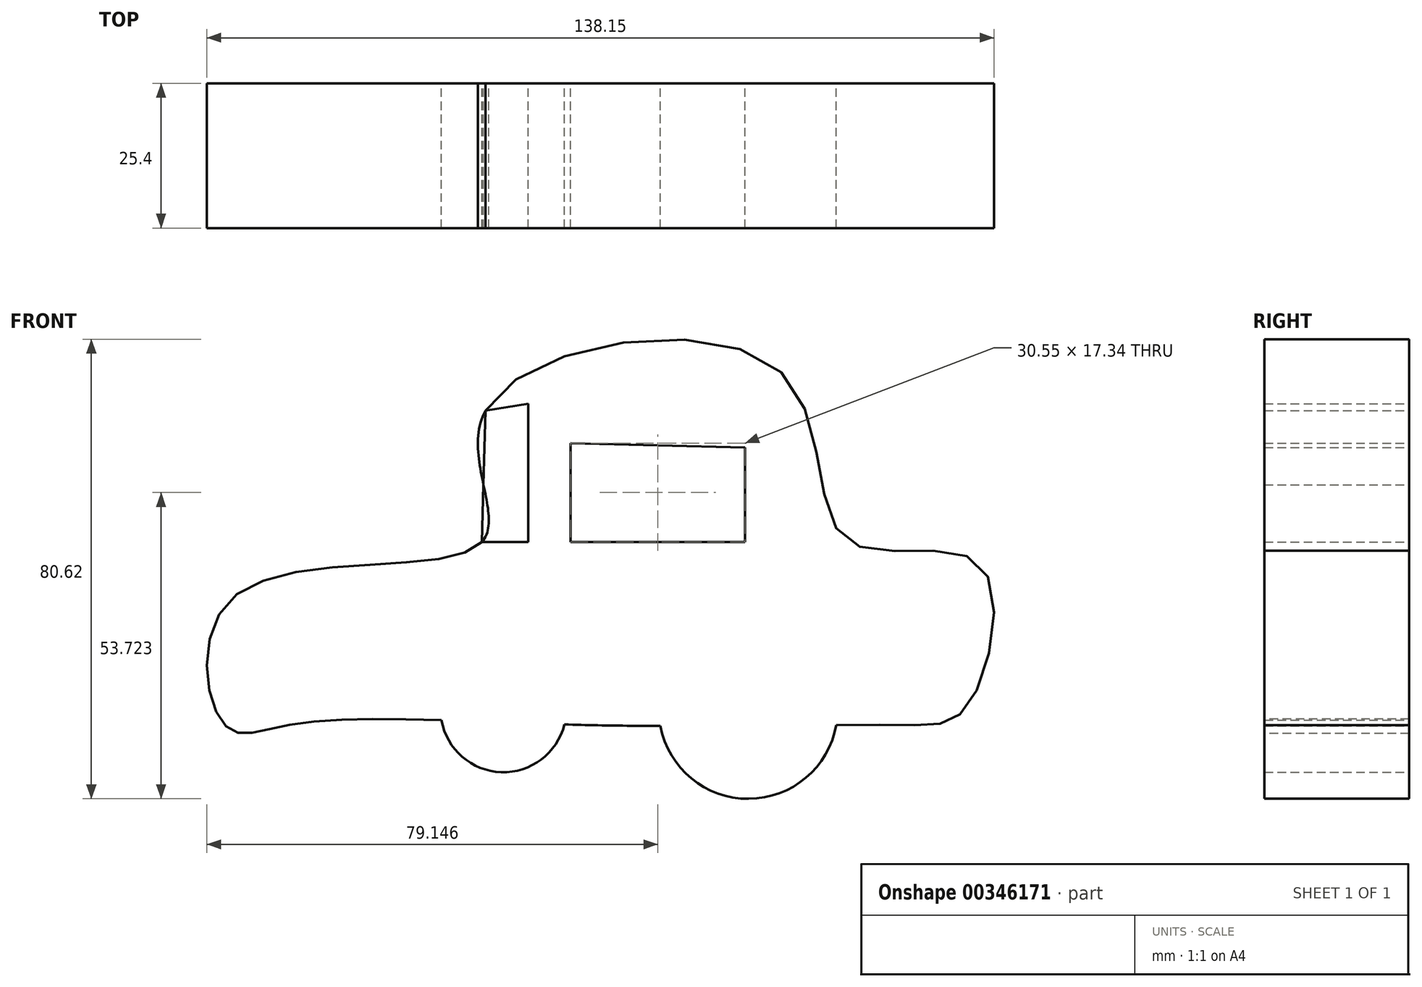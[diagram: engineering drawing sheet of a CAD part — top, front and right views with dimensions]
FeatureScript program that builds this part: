
annotation { "Feature Type Name" : "Feature", "Feature Type Description" : "" }
export const myFeature = defineFeature(function(context is Context, id is Id, definition is map)
    precondition{}
    {
        {
            var Q0;
            Q0=qCreatedBy(makeId("Front.planeOp"),FACE);
            var sketch = newSketch(context, id + "F0", { "sketchPlane" : qUnion([Q0])});
            skFitSpline(sketch, "E0", {"points": [v(-75.67, 0) * mm, v(-73.9, 22.66) * mm, v(-30.55, 32.12) * mm, v(-29.95, 55.18) * mm, v(21.09, 62.67) * mm, v(33.3, 32.52) * mm, v(56.56, 28.38) * mm, v(54.79, 3.55) * mm, v(43.55, 0) * mm, v(-11.82, 0) * mm, v(-64.44, 0) * mm, v(-75.67, 0) * mm]});
            skCircle(sketch, "E1", {"center": v(-26.8, 2.76) * mm, "radius": 11.03 * mm});
            skCircle(sketch, "E2", {"center": v(16.16, 2.76) * mm, "radius": 15.7 * mm});
            skLineSegment(sketch, "E3", {"start": v(-30.55, 32.12) * mm, "end": v(-22.47, 32.12) * mm});
            skLineSegment(sketch, "E4", {"start": v(-22.47, 32.12) * mm, "end": v(-22.47, 56.36) * mm});
            skLineSegment(sketch, "E5", {"start": v(-22.47, 56.36) * mm, "end": v(-29.95, 55.18) * mm});
            skLineSegment(sketch, "E6", {"start": v(-29.95, 55.18) * mm, "end": v(-30.55, 32.12) * mm});
            skLineSegment(sketch, "E7", {"start": v(-14.98, 49.46) * mm, "end": v(-14.98, 32.12) * mm});
            skLineSegment(sketch, "E8", {"start": v(-14.98, 32.12) * mm, "end": v(15.57, 32.12) * mm});
            skLineSegment(sketch, "E9", {"start": v(15.57, 32.12) * mm, "end": v(15.57, 48.68) * mm});
            skLineSegment(sketch, "E10", {"start": v(15.57, 48.68) * mm, "end": v(-14.98, 49.46) * mm});
            skSolve(sketch);
        }
        {
            var Q0;
            {var subQ0=sQuery(id+"F0.wireOp",EDGE,"E6");var subQ1=sQuery(id+"F0.wireOp",EDGE,"E0");var subQ3=makeQuery(id+"F0.imprint","INTERSECT",VERTEX,{"derivedFrom":[subQ1,subQ0]});Q0=makeQuery(id+"F0.imprint","IMPRINT",FACE,{"disambiguationData":[TD([[makeQuery(id+"F0.imprint","IMPRINT",EDGE,{"disambiguationData":[TD([[subQ3,1.0]])],"derivedFrom":subQ1}),1.0]])]});}
            var Q1;
            {var subQ0=sQuery(id+"F0.wireOp",EDGE,"E6");var subQ1=sQuery(id+"F0.wireOp",EDGE,"E0");var subQ3=makeQuery(id+"F0.imprint","INTERSECT",VERTEX,{"derivedFrom":[subQ1,subQ0]});Q1=makeQuery(id+"F0.imprint","IMPRINT",FACE,{"disambiguationData":[TD([[makeQuery(id+"F0.imprint","IMPRINT",EDGE,{"disambiguationData":[TD([[subQ3,-1.0]])],"derivedFrom":subQ1}),-1.0]])]});}
            var Q2;
            {var subQ0=sQuery(id+"F0.wireOp",EDGE,"E2");var subQ1=sQuery(id+"F0.wireOp",EDGE,"E0");var subQ2=makeQuery(id+"F0.imprint","INTERSECT",VERTEX,{"disambiguationData":[OD(0.0)],"derivedFrom":[subQ1,subQ0]});Q2=makeQuery(id+"F0.imprint","IMPRINT",FACE,{"disambiguationData":[TD([[makeQuery(id+"F0.imprint","IMPRINT",EDGE,{"disambiguationData":[TD([[subQ2,-1.0]])],"derivedFrom":subQ1}),1.0]])]});}
            var Q3;
            {var subQ0=sQuery(id+"F0.wireOp",EDGE,"E1");var subQ1=sQuery(id+"F0.wireOp",EDGE,"E0");var subQ2=makeQuery(id+"F0.imprint","INTERSECT",VERTEX,{"disambiguationData":[OD(0.0)],"derivedFrom":[subQ1,subQ0]});Q3=makeQuery(id+"F0.imprint","IMPRINT",FACE,{"disambiguationData":[TD([[makeQuery(id+"F0.imprint","IMPRINT",EDGE,{"disambiguationData":[TD([[subQ2,-1.0]])],"derivedFrom":subQ1}),1.0]])]});}
            var Q4;
            {var subQ0=sQuery(id+"F0.wireOp",EDGE,"E2");var subQ1=sQuery(id+"F0.wireOp",EDGE,"E0");var subQ2=makeQuery(id+"F0.imprint","INTERSECT",VERTEX,{"disambiguationData":[OD(0.0)],"derivedFrom":[subQ1,subQ0]});Q4=makeQuery(id+"F0.imprint","IMPRINT",FACE,{"disambiguationData":[TD([[makeQuery(id+"F0.imprint","IMPRINT",EDGE,{"disambiguationData":[TD([[subQ2,-1.0]])],"derivedFrom":subQ1}),-1.0]])]});}
            var Q5;
            {var subQ0=sQuery(id+"F0.wireOp",EDGE,"E1");var subQ1=sQuery(id+"F0.wireOp",EDGE,"E0");var subQ2=makeQuery(id+"F0.imprint","INTERSECT",VERTEX,{"disambiguationData":[OD(0.0)],"derivedFrom":[subQ1,subQ0]});Q5=makeQuery(id+"F0.imprint","IMPRINT",FACE,{"disambiguationData":[TD([[makeQuery(id+"F0.imprint","IMPRINT",EDGE,{"disambiguationData":[TD([[subQ2,-1.0]])],"derivedFrom":subQ1}),-1.0]])]});}
            var Q6;
            {var subQ0=sQuery(id+"F0.wireOp",EDGE,"E3");Q6=makeQuery(id+"F0.imprint","IMPRINT",FACE,{"disambiguationData":[TD([[makeQuery(id+"F0.imprint","IMPRINT",EDGE,{"derivedFrom":subQ0}),-1.0]])]});}
            extrude(context, id + "F1", {"entities" : qUnion([Q0, Q1, Q2, Q3, Q4, Q5, Q6]), "depth" : 25.4 * mm});
        }
    });
